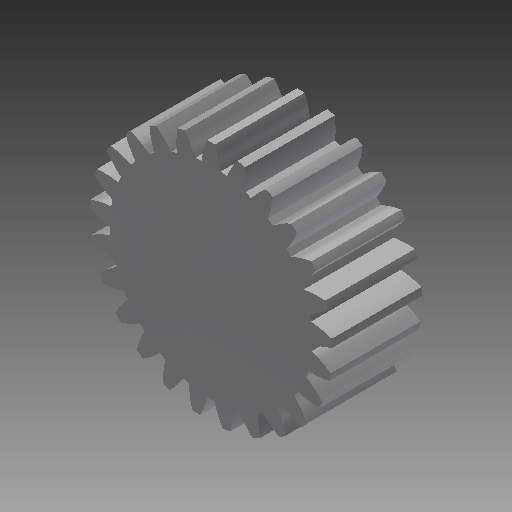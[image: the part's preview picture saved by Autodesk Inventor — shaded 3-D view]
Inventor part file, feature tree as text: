
AUTODESK INVENTOR PART (.ipt)
format: ipt  version: 2019 (Build 230136000, 136)  size: 246,272 bytes
history: native  units: mm (DEFAULTED — no unit token found)
features: plane x3, other x3, sketch x2, extrude x1
ambient origin geometry x8: Origin, YZ Plane, XZ Plane, XY Plane, X Axis, Y Axis, Z Axis, Center Point
bodies: Solid1 (feature_tree)
feature tree (9):
  extrude  "Extrusion1"  Depth=20.0mm TaperAngle=0.0deg
  plane  "Work Plane2"
  plane  "Work Plane8"
  plane  "Work Plane9"
  other  "Цилиндрическое зубчатое зацепление"
  sketch  "Sketch1"  dims[d0=54.0mm d1=20.0mm d2=0.0mm]
  sketch  "Sketch2"  dims[d3=50.0mm d4=10.0mm d5=0.0mm d16=50.0mm d17=0.0mm d34=1.256637mm d39=0.0mm d41=0.0mm d43=50.0mm d46=50.0mm d47=0.0mm d48=0.0mm]
  other  "Srf1"
  other  "Средний диаметр"
